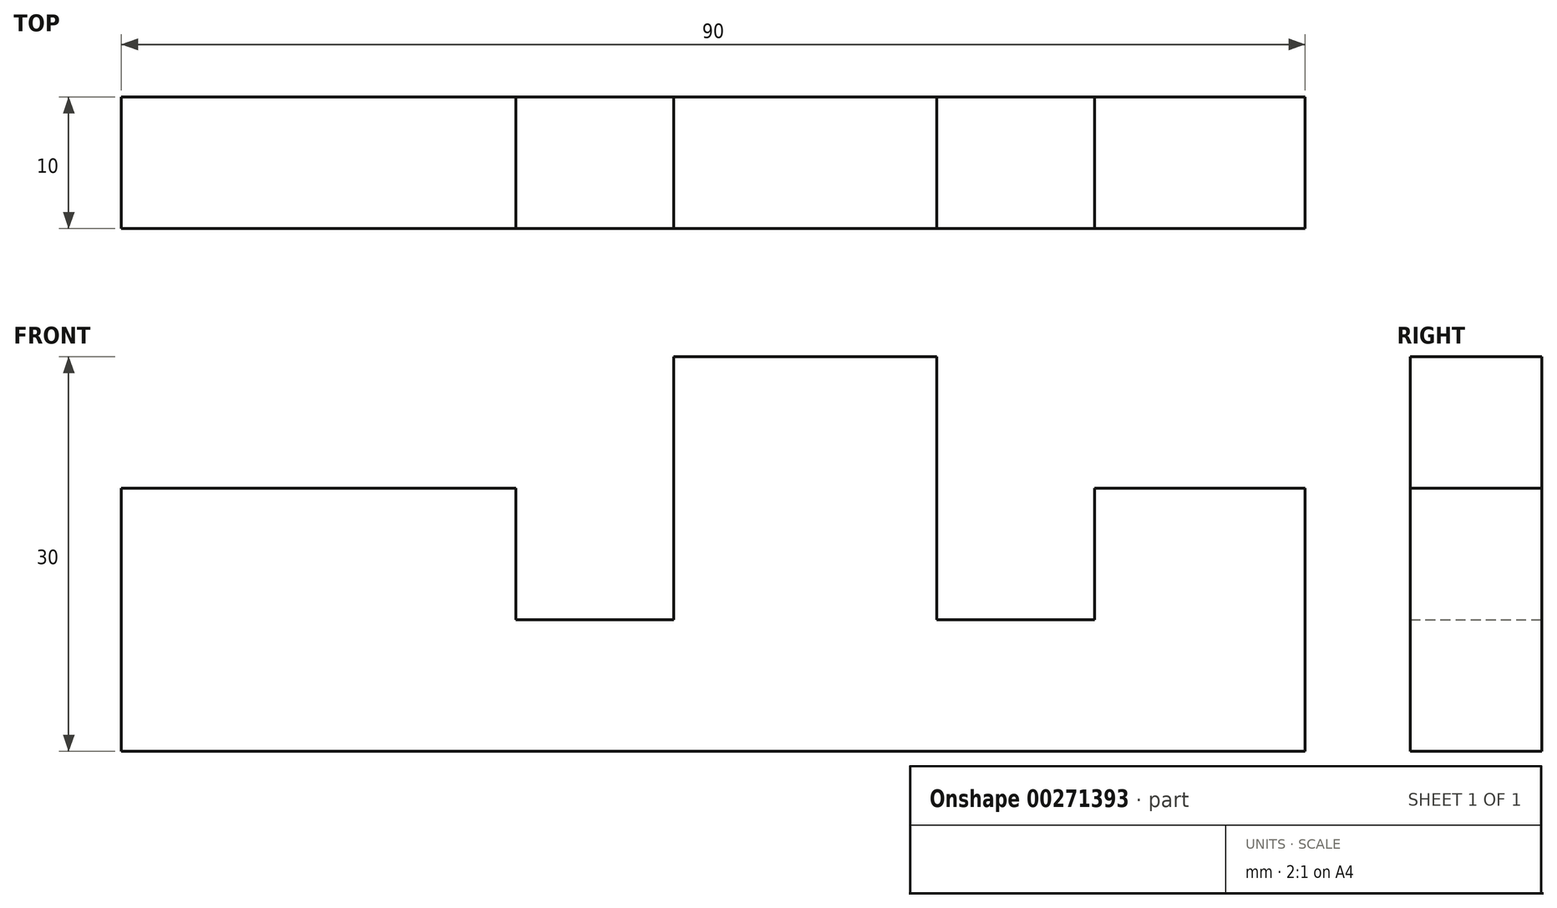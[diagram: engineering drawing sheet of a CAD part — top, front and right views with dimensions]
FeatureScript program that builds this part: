
annotation { "Feature Type Name" : "Feature", "Feature Type Description" : "" }
export const myFeature = defineFeature(function(context is Context, id is Id, definition is map)
    precondition{}
    {
        {
            var Q0;
            Q0=qCreatedBy(makeId("Front.planeOp"),FACE);
            var sketch = newSketch(context, id + "F0", { "sketchPlane" : qUnion([Q0])});
            skLineSegment(sketch, "E0", {"start": v(0, 0) * mm, "end": v(90, 0) * mm});
            skLineSegment(sketch, "E1", {"start": v(90, 0) * mm, "end": v(90, 20) * mm});
            skLineSegment(sketch, "E2", {"start": v(90, 20) * mm, "end": v(74, 20) * mm});
            skLineSegment(sketch, "E3", {"start": v(74, 20) * mm, "end": v(74, 10) * mm});
            skLineSegment(sketch, "E4", {"start": v(74, 10) * mm, "end": v(62, 10) * mm});
            skLineSegment(sketch, "E5", {"start": v(62, 10) * mm, "end": v(62, 30) * mm});
            skLineSegment(sketch, "E6", {"start": v(62, 30) * mm, "end": v(42, 30) * mm});
            skLineSegment(sketch, "E7", {"start": v(42, 30) * mm, "end": v(42, 10) * mm});
            skLineSegment(sketch, "E8", {"start": v(30, 10) * mm, "end": v(30, 20) * mm});
            skLineSegment(sketch, "E9", {"start": v(30, 20) * mm, "end": v(0, 20) * mm});
            skLineSegment(sketch, "E10", {"start": v(0, 20) * mm, "end": v(0, 0) * mm});
            skLineSegment(sketch, "E11", {"start": v(30, 10) * mm, "end": v(42, 10) * mm});
            skSolve(sketch);
        }
        {
            var Q0;
            Q0 = qSketchRegion(id + "F0", true);
            extrude(context, id + "F1", {"entities" : qUnion([Q0]), "depth" : 10 * mm});
        }
    });
